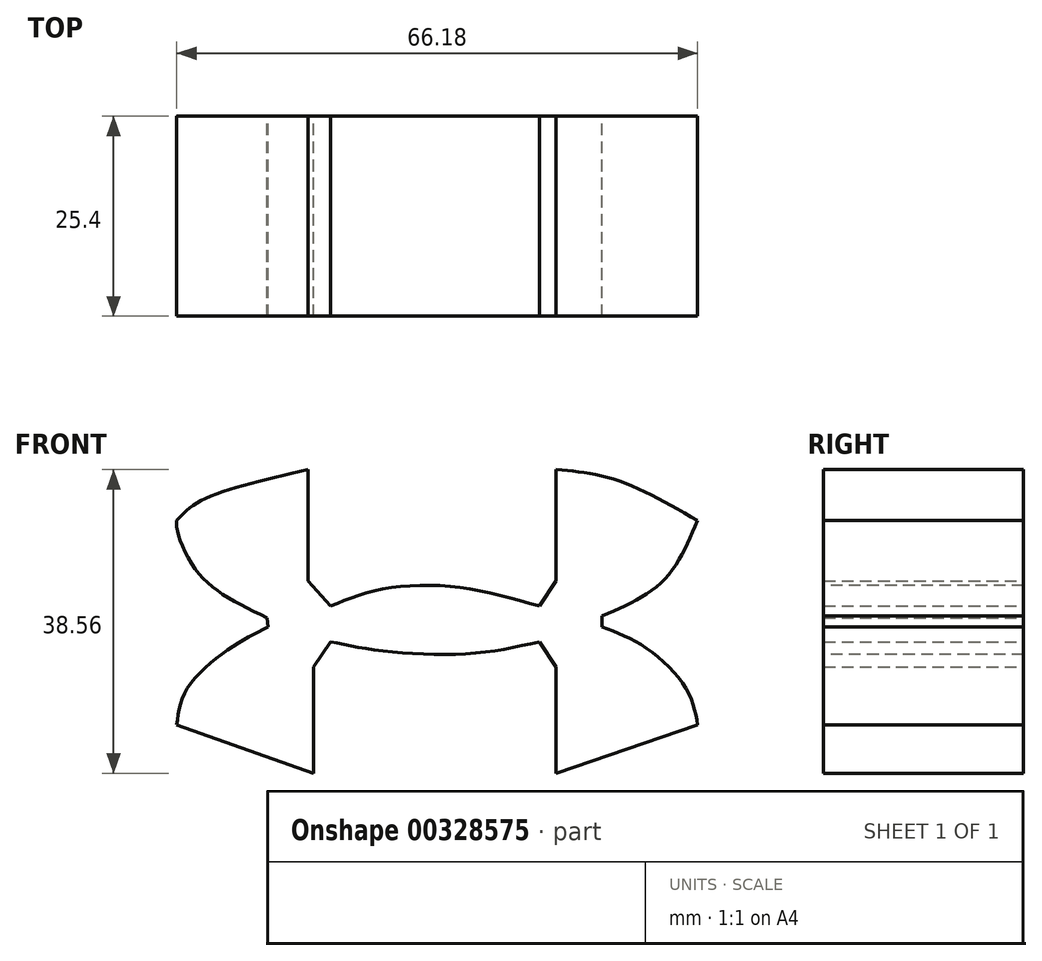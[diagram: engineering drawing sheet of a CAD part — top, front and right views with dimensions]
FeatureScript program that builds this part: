
annotation { "Feature Type Name" : "Feature", "Feature Type Description" : "" }
export const myFeature = defineFeature(function(context is Context, id is Id, definition is map)
    precondition{}
    {
        {
            var Q0;
            Q0=qCreatedBy(makeId("Front.planeOp"),FACE);
            var sketch = newSketch(context, id + "F0", { "sketchPlane" : qUnion([Q0])});
            skFitSpline(sketch, "E0", {"points": [v(-21.6, 5.98) * mm, v(-27.35, 9.06) * mm, v(-30.89, 12.44) * mm, v(-32.94, 16.7) * mm, v(-33.1, 18.35) * mm], "startDerivative": vector(-19.8, 9.54) * mm, "endDerivative": vector(0.14, 9.28) * mm});
            skFitSpline(sketch, "E1", {"points": [v(-33.1, 18.35) * mm, v(-30.02, 20.87) * mm, v(-16.4, 24.8) * mm], "startDerivative": vector(6.8, 7.5) * mm, "endDerivative": vector(24.75, 5.61) * mm});
            skFitSpline(sketch, "E2", {"points": [v(-16.4, 24.8) * mm, v(-16.4, 10.7) * mm], "startDerivative": vector(0, -14.1) * mm, "endDerivative": vector(0, -14.1) * mm});
            skFitSpline(sketch, "E3", {"points": [v(-16.4, 10.7) * mm, v(-13.56, 7.48) * mm], "startDerivative": vector(2.84, -3.23) * mm, "endDerivative": vector(2.84, -3.23) * mm});
            skFitSpline(sketch, "E4", {"points": [v(-13.56, 7.48) * mm, v(-7.5, 9.53) * mm, v(2.27, 9.92) * mm, v(12.98, 7.48) * mm], "startDerivative": vector(20, 8.28) * mm, "endDerivative": vector(28.76, -8.28) * mm});
            skFitSpline(sketch, "E5", {"points": [v(12.98, 7.48) * mm, v(15.11, 10.7) * mm], "startDerivative": vector(2.13, 3.23) * mm, "endDerivative": vector(2.13, 3.23) * mm});
            skFitSpline(sketch, "E6", {"points": [v(15.11, 10.7) * mm, v(15.11, 24.8) * mm], "startDerivative": vector(0, 14.1) * mm, "endDerivative": vector(0, 14.1) * mm});
            skFitSpline(sketch, "E7", {"points": [v(15.11, 24.8) * mm, v(22.57, 23.57) * mm, v(33.08, 18.35) * mm], "startDerivative": vector(16.26, -1.31) * mm, "endDerivative": vector(19.56, -11.24) * mm});
            skFitSpline(sketch, "E8", {"points": [v(33.08, 18.35) * mm, v(28.68, 10.7) * mm, v(20.94, 6.21) * mm], "startDerivative": vector(-7.2, -16.93) * mm, "endDerivative": vector(-17.07, -7.35) * mm});
            skFitSpline(sketch, "E9", {"points": [v(20.94, 6.21) * mm, v(20.94, 4.83) * mm], "startDerivative": vector(0, -1.38) * mm, "endDerivative": vector(0, -1.38) * mm});
            skFitSpline(sketch, "E10", {"points": [v(20.94, 4.83) * mm, v(26.32, 2.3) * mm, v(31.7, -3.15) * mm, v(33.08, -7.64) * mm], "startDerivative": vector(16.07, -5.94) * mm, "endDerivative": vector(2.56, -14.99) * mm});
            skFitSpline(sketch, "E11", {"points": [v(33.08, -7.64) * mm, v(15.11, -13.75) * mm], "startDerivative": vector(-17.97, -6.11) * mm, "endDerivative": vector(-17.97, -6.11) * mm});
            skFitSpline(sketch, "E12", {"points": [v(15.11, -13.75) * mm, v(15.11, -0.22) * mm], "startDerivative": vector(0, 13.52) * mm, "endDerivative": vector(0, 13.52) * mm});
            skFitSpline(sketch, "E13", {"points": [v(15.11, -0.22) * mm, v(12.98, 2.96) * mm], "startDerivative": vector(-2.13, 3.18) * mm, "endDerivative": vector(-2.13, 3.18) * mm});
            skFitSpline(sketch, "E14", {"points": [v(12.98, 2.96) * mm, v(3.67, 1.4) * mm, v(-7.65, 1.9) * mm, v(-13.56, 2.96) * mm], "startDerivative": vector(-25.55, -5.78) * mm, "endDerivative": vector(-19.33, 4.08) * mm});
            skFitSpline(sketch, "E15", {"points": [v(-13.56, 2.96) * mm, v(-15.72, -0.22) * mm], "startDerivative": vector(-2.16, -3.18) * mm, "endDerivative": vector(-2.16, -3.18) * mm});
            skFitSpline(sketch, "E16", {"points": [v(-15.72, -0.22) * mm, v(-15.72, -13.75) * mm], "startDerivative": vector(0, -13.52) * mm, "endDerivative": vector(0, -13.52) * mm});
            skFitSpline(sketch, "E17", {"points": [v(-15.72, -13.75) * mm, v(-33.1, -7.64) * mm], "startDerivative": vector(-17.38, 6.11) * mm, "endDerivative": vector(-17.38, 6.11) * mm});
            skFitSpline(sketch, "E18", {"points": [v(-33.1, -7.64) * mm, v(-31.77, -3) * mm, v(-26.15, 2.22) * mm, v(-21.5, 4.83) * mm], "startDerivative": vector(1.9, 15.41) * mm, "endDerivative": vector(13.9, 6.98) * mm});
            skFitSpline(sketch, "E19", {"points": [v(-21.5, 4.83) * mm, v(-21.6, 5.98) * mm], "startDerivative": vector(-0.1, 1.15) * mm, "endDerivative": vector(-0.1, 1.15) * mm});
            skFitSpline(sketch, "E20", {"points": [v(9.44, 5.98) * mm, v(1.86, 7.48) * mm, v(-7.65, 7.48) * mm, v(-11.52, 5.98) * mm], "startDerivative": vector(-30.3, 10.64) * mm, "endDerivative": vector(-12.83, -6.82) * mm});
            skFitSpline(sketch, "E21", {"points": [v(-11.52, 5.98) * mm, v(-11.52, 4.85) * mm, v(-3.97, 3.12) * mm, v(6.38, 3.62) * mm, v(9.59, 4.52) * mm], "startDerivative": vector(-3.34, -9.84) * mm, "endDerivative": vector(13.27, 4.7) * mm});
            skFitSpline(sketch, "E22", {"points": [v(9.5, 4.68) * mm, v(9.44, 5.98) * mm], "startDerivative": vector(-0.06, 1.3) * mm, "endDerivative": vector(-0.06, 1.3) * mm});
            skSolve(sketch);
        }
        {
            var Q0;
            Q0 = qSketchRegion(id + "F0", true);
            extrude(context, id + "F1", {"entities" : qUnion([Q0]), "depth" : 25.4 * mm});
        }
    });
